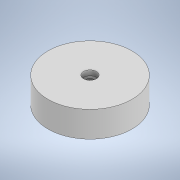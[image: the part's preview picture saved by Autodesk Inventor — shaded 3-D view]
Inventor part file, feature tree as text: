
AUTODESK INVENTOR PART (.ipt)
format: ipt  version: 2020 (Build 240168000, 168)  size: 102,400 bytes
history: native  units: mm
features: sketch x2, extrude x1, hole x1
ambient origin geometry x8: Origin, YZ Plane, XZ Plane, XY Plane, X Axis, Y Axis, Z Axis, Center Point
bodies: Solid1 (feature_tree)
feature tree (4):
  extrude  "Extrusion1"  Depth=20.0mm TaperAngle=0.0deg
  hole  "Hole1"  [1 undecoded]
  sketch  "Sketch1"  dims[d0=65.0mm d1=20.0mm d2=0.0mm]
  sketch  "Sketch2"  dims[d3=5.2mm d4=6.0mm d5=10.0mm d6=4.0mm d7=90.0deg d8=18.0mm d9=0.0mm]
note: 1 required parameter value undecoded (feature->parameter linkage not recoverable at this tier; creation-order binding heuristic only, values carry confidence <= 0.55)
